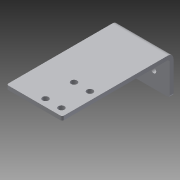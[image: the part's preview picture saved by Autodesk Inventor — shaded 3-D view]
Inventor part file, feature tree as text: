
AUTODESK INVENTOR PART (.ipt)
format: ipt  version: 2014 (Build 180170000, 170)  size: 130,560 bytes
history: native  units: in
note: dims shown in document units (in); Inventor stores cm internally (conversion verified against a paired STEP export)
features: sheet_metal_op x4, sketch x3, other x2, fillet x1, extrude x1
ambient origin geometry x8: Origin, YZ Plane, XZ Plane, XY Plane, X Axis, Y Axis, Z Axis, Center Point
bodies: Solid1 (feature_tree)
feature tree (11):
  sheet_metal_op  "Face1"
  sheet_metal_op  "Flange1"
  fillet  "Fillet1"  Radius=1.75in
  extrude  "Extrusion1"  Depth=0.163in
  sketch  "Sketch1"  dims[d1=1.0in d2=0.163in]
  other  "Plate1"
  sketch  "Sketch2"  dims[d4=0.7874in d6=1.0in d7=0.3937in d9=1.0in]
  other  "Plate2"
  sheet_metal_op  "Bend1"
  sheet_metal_op  "Corner1"
  sketch  "Sketch3"  dims[d11=0.125in d12=0.125in d13=0.0625in d14=0.25in d15=0.125in d16=3.5in d17=90.0deg d18=0.05in d19=0.5in d20=0.125in d21=0.125in d22=0.0625in d23=1.35in d24=0.75in d27=0.19in d28=0.125in d29=0.2265in d30=1.0in d31=0.0in d34=0.25in d35=0.875in]
